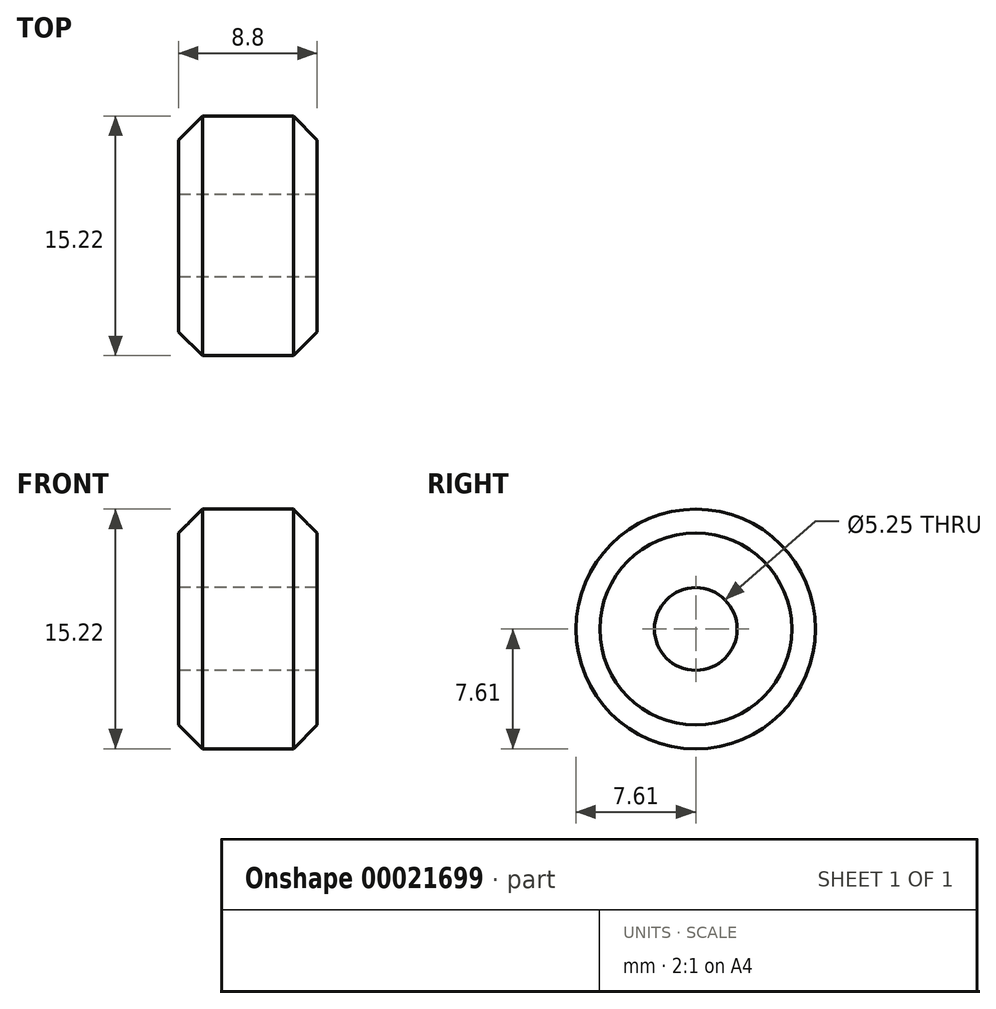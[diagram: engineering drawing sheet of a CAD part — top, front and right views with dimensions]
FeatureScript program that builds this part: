
annotation { "Feature Type Name" : "Feature", "Feature Type Description" : "" }
export const myFeature = defineFeature(function(context is Context, id is Id, definition is map)
    precondition{}
    {
        {
            var Q0;
            Q0=qCreatedBy(makeId("Top.planeOp"),FACE);
            var sketch = newSketch(context, id + "F0", { "sketchPlane" : qUnion([Q0])});
            skLineSegment(sketch, "E0.bottom", {"start": v(0, 0) * mm, "end": v(4.4, 0) * mm, "construction": true});
            skLineSegment(sketch, "E1.bottom", {"start": v(0, 2.62) * mm, "end": v(4.4, 2.62) * mm});
            skLineSegment(sketch, "E1.top", {"start": v(0, 7.6) * mm, "end": v(2.89, 7.61) * mm});
            skLineSegment(sketch, "E1.left", {"start": v(0, 2.63) * mm, "end": v(0, 7.61) * mm, "construction": true});
            skLineSegment(sketch, "E1.right", {"start": v(4.4, 2.63) * mm, "end": v(4.4, 6.1) * mm});
            skLineSegment(sketch, "E2", {"start": v(4.4, 6.1) * mm, "end": v(2.89, 7.61) * mm});
            skPoint(sketch, "E3.orphan", {"position": v(4.4, 7.61) * mm});
            skLineSegment(sketch, "E4", {"start": v(0, 2.62) * mm, "end": v(0, 0) * mm, "construction": true});
            skLineSegment(sketch, "E5.MirrorCS", {"start": v(0, 7.6) * mm, "end": v(-2.89, 7.61) * mm});
            skLineSegment(sketch, "E6.MirrorCS", {"start": v(-4.4, 6.1) * mm, "end": v(-2.89, 7.61) * mm});
            skLineSegment(sketch, "E7.MirrorCS", {"start": v(-4.4, 2.63) * mm, "end": v(-4.4, 6.1) * mm});
            skLineSegment(sketch, "E8.MirrorCS", {"start": v(0, 2.62) * mm, "end": v(-4.4, 2.62) * mm});
            skSolve(sketch);
        }
        {
            var Q0;
            Q0=makeQuery(id+"F0.imprint","IMPRINT",FACE,{"disambiguationData":[TD([[makeQuery(id+"F0.imprint","IMPRINT",EDGE,{"derivedFrom":sQuery(id+"F0.wireOp",EDGE,"E1.top")}),-1.0]])]});
            var Q1;
            Q1=sQuery(id+"F0.wireOp",EDGE,"E0.bottom");
            revolve(context, id + "F1", {"entities" : qUnion([Q0]), "axis" : qUnion([Q1]), "revolveType" : RevolveType.FULL});
        }
    });
